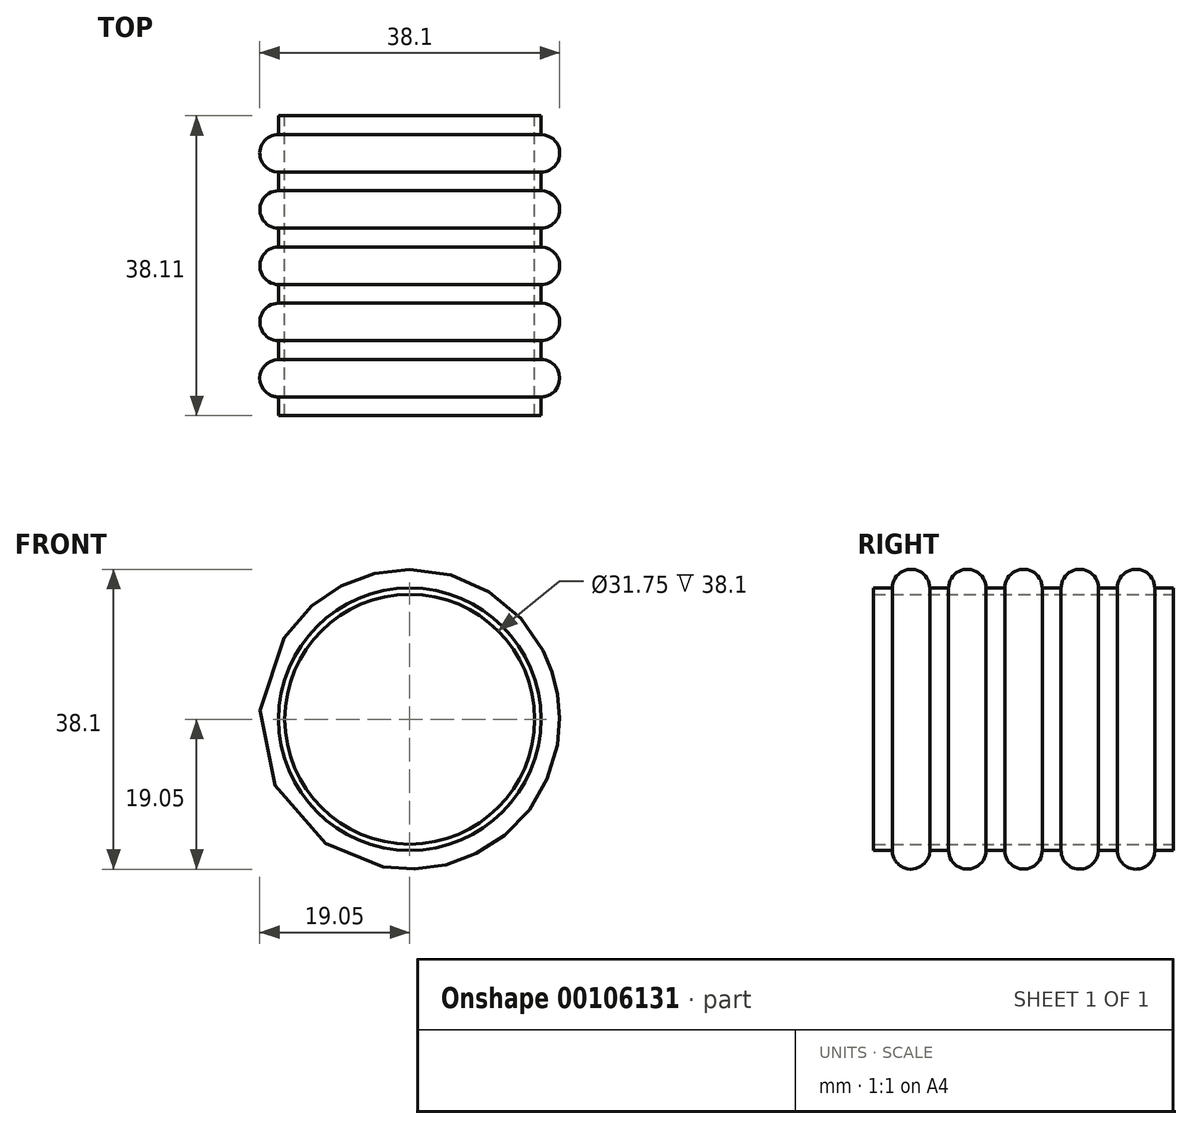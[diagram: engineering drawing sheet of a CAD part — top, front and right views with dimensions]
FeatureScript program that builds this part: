
annotation { "Feature Type Name" : "Feature", "Feature Type Description" : "" }
export const myFeature = defineFeature(function(context is Context, id is Id, definition is map)
    precondition{}
    {
        {
            var Q0;
            Q0=qCreatedBy(makeId("Right.planeOp"),FACE);
            var sketch = newSketch(context, id + "F0", { "sketchPlane" : qUnion([Q0])});
            skLineSegment(sketch, "E0", {"start": v(152.4, 0) * mm, "end": v(-152.4, 0) * mm, "construction": true});
            skLineSegment(sketch, "E1", {"start": v(-22.23, 0) * mm, "end": v(-22.23, 15.88) * mm, "construction": true});
            skLineSegment(sketch, "E2", {"start": v(-41.28, 15.88) * mm, "end": v(-3.18, 15.88) * mm});
            skLineSegment(sketch, "E3", {"start": v(-41.28, 15.88) * mm, "end": v(-41.28, 16.67) * mm});
            skLineSegment(sketch, "E4", {"start": v(-41.28, 16.67) * mm, "end": v(-38.9, 16.67) * mm});
            skLineSegment(sketch, "E5", {"start": v(-3.18, 16.67) * mm, "end": v(-3.18, 15.88) * mm});
            skArc(sketch, "E6", {"start": v(-19.84, 16.67) * mm, "mid": v(-22.23, 19.05) * mm, "end": v(-24.6, 16.67) * mm});
            skLineSegment(sketch, "E7.trimOffspring", {"start": v(-19.84, 16.67) * mm, "end": v(-17.46, 16.67) * mm});
            skArc(sketch, "E8.1.0.0", {"start": v(-12.7, 16.67) * mm, "mid": v(-15.08, 19.05) * mm, "end": v(-17.46, 16.67) * mm});
            skArc(sketch, "E8.2.0.0", {"start": v(-5.56, 16.67) * mm, "mid": v(-7.94, 19.05) * mm, "end": v(-10.32, 16.67) * mm});
            skLineSegment(sketch, "E8.direction1", {"start": v(-24.6, 16.67) * mm, "end": v(-17.46, 16.67) * mm, "construction": true});
            skLineSegment(sketch, "E9.trimOffspring", {"start": v(-12.7, 16.67) * mm, "end": v(-10.32, 16.67) * mm});
            skLineSegment(sketch, "E10.trimOffspring", {"start": v(-5.56, 16.67) * mm, "end": v(-3.18, 16.67) * mm});
            skArc(sketch, "E11.MirrorCS", {"start": v(-31.75, 16.67) * mm, "mid": v(-29.37, 19.05) * mm, "end": v(-26.99, 16.67) * mm});
            skArc(sketch, "E12.MirrorCS", {"start": v(-38.9, 16.67) * mm, "mid": v(-36.51, 19.05) * mm, "end": v(-34.13, 16.67) * mm});
            skLineSegment(sketch, "E13.trimOffspring", {"start": v(-34.13, 16.67) * mm, "end": v(-31.75, 16.67) * mm});
            skLineSegment(sketch, "E14.trimOffspring", {"start": v(-26.99, 16.67) * mm, "end": v(-24.6, 16.67) * mm});
            skSolve(sketch);
        }
        {
            var Q0;
            Q0 = qSketchRegion(id + "F0", true);
            var Q1;
            Q1=sQuery(id+"F0.wireOp",EDGE,"E0");
            revolve(context, id + "F1", {"entities" : qUnion([Q0]), "axis" : qUnion([Q1]), "revolveType" : RevolveType.FULL});
        }
    });
